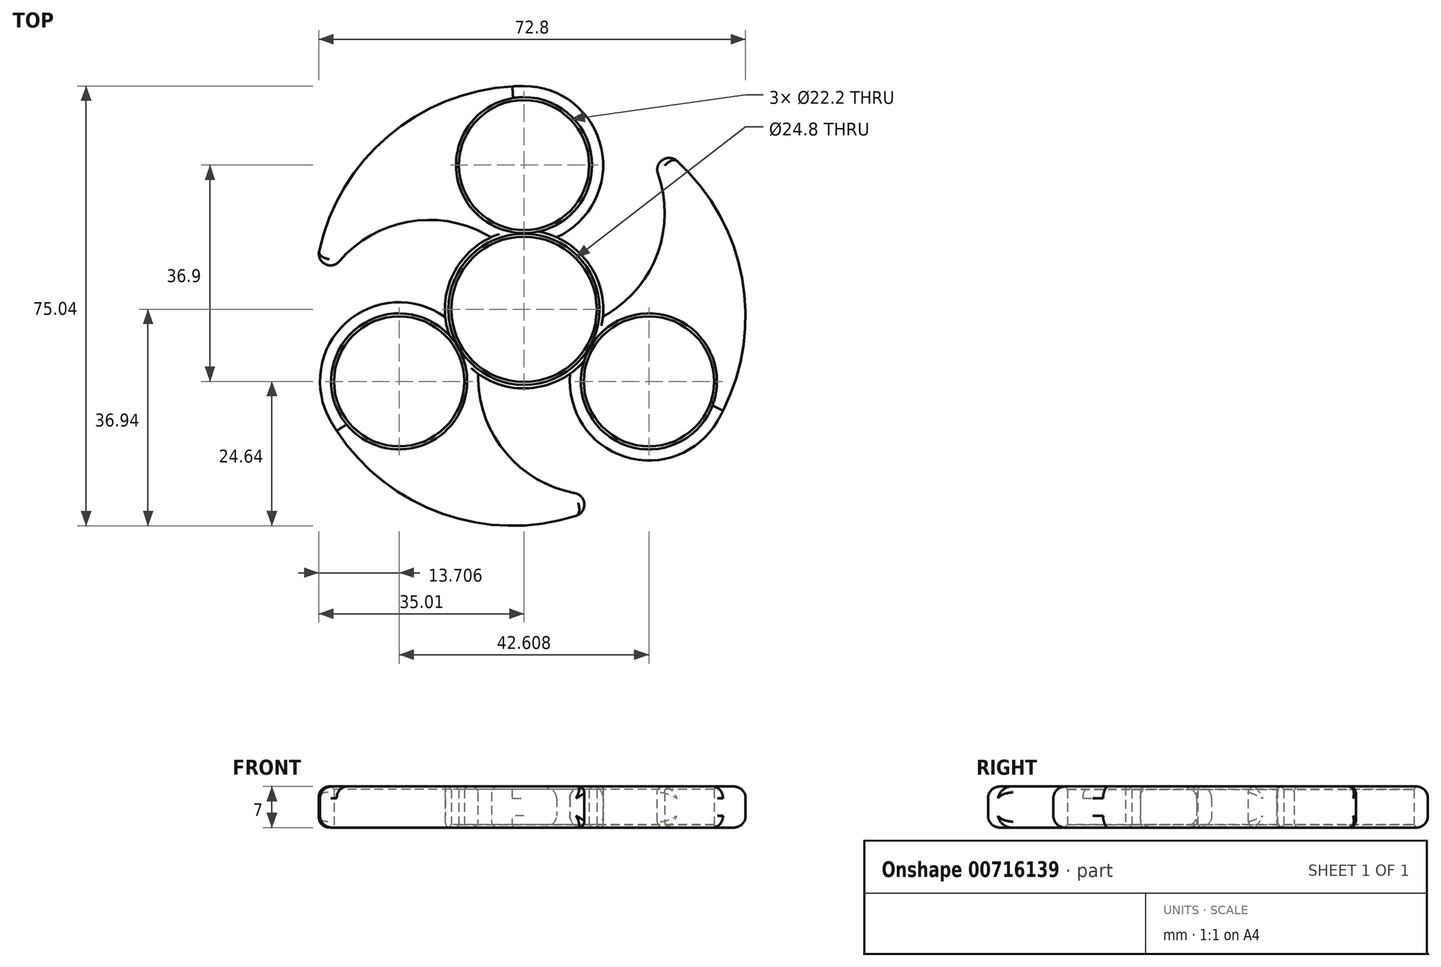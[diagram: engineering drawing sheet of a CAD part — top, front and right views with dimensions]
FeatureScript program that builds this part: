
annotation { "Feature Type Name" : "Feature", "Feature Type Description" : "" }
export const myFeature = defineFeature(function(context is Context, id is Id, definition is map)
    precondition{}
    {
        {
            var Q0;
            Q0=qCreatedBy(makeId("Top.planeOp"),FACE);
            var sketch = newSketch(context, id + "F0", { "sketchPlane" : qUnion([Q0])});
            skCircle(sketch, "E0", {"center": v(0, 0) * mm, "radius": 12.3 * mm});
            skCircle(sketch, "E1", {"center": v(0, 0) * mm, "radius": 4 * mm});
            skCircle(sketch, "E2", {"center": v(0, 0) * mm, "radius": 12.4 * mm});
            skCircle(sketch, "E3", {"center": v(0, 27.4) * mm, "radius": 11.2 * mm});
            skCircle(sketch, "E4", {"center": v(0, 0) * mm, "radius": 15 * mm});
            skCircle(sketch, "E5", {"center": v(0, 27.4) * mm, "radius": 15 * mm});
            skSolve(sketch);
        }
        {
            var Q0;
            Q0=qCreatedBy(makeId("Top.planeOp"),FACE);
            var sketch = newSketch(context, id + "F1", { "sketchPlane" : qUnion([Q0])});
            skCircle(sketch, "E6.0", {"center": v(0, 24.6) * mm, "radius": 11.1 * mm});
            skArc(sketch, "E6.1", {"start": v(5.56, 12.3) * mm, "mid": v(0, 38.1) * mm, "end": v(-5.56, 12.3) * mm});
            skArc(sketch, "E6.2", {"start": v(-5.56, 12.3) * mm, "mid": v(0, -13.5) * mm, "end": v(5.56, 12.3) * mm});
            skCircle(sketch, "E6.3", {"center": v(0, 0) * mm, "radius": 12.4 * mm});
            skSolve(sketch);
        }
        {
            var Q0;
            Q0=qSketchRegion(id+"F1",true);
            extrude(context, id + "F2", {"entities" : qUnion([Q0]), "depth" : 7 * mm, "offsetDistance" : 25 * mm});
        }
        {
            var Q0;
            Q0=makeQuery(id+"F2.opExtrude","SWEPT_BODY",BODY,{"disambiguationData":[OSD([sQuery(id+"F1.wireOp",EDGE,"E6.0"),sQuery(id+"F1.wireOp",EDGE,"E6.1"),sQuery(id+"F1.wireOp",EDGE,"E6.2"),sQuery(id+"F1.wireOp",EDGE,"E6.3")])]});
            var Q1;
            Q1=makeQuery(id+"F2.opExtrude","CAP_EDGE",EDGE,{"disambiguationData":[OSD([sQuery(id+"F1.wireOp",EDGE,"E6.3")])],"isStart":false});
            circularPattern(context, id + "F3", {"operationType" : NewBodyOperationType.ADD, "entities" : qUnion([Q0]), "axis" : qUnion([Q1]), "angle" : 360 * degree, "instanceCount" : 3, "equalSpace" : true});
        }
        {
            var Q0;
            Q0=qCreatedBy(makeId("Top.planeOp"),FACE);
            var sketch = newSketch(context, id + "F4", { "sketchPlane" : qUnion([Q0])});
            skArc(sketch, "E7", {"start": v(0, 38.1) * mm, "mid": v(-26.1, 26.79) * mm, "end": v(-35.7, 0) * mm});
            skLineSegment(sketch, "E8", {"start": v(0, 0) * mm, "end": v(0, 35.7) * mm, "construction": true});
            skLineSegment(sketch, "E9", {"start": v(0, 0) * mm, "end": v(-35.7, 0) * mm, "construction": true});
            skArc(sketch, "E10", {"start": v(-6.5, 12.77) * mm, "mid": v(-24.24, 13.57) * mm, "end": v(-35.7, 0) * mm});
            skLineSegment(sketch, "E11", {"start": v(1, 25.76) * mm, "end": v(-6.5, 12.77) * mm, "construction": true});
            skArc(sketch, "E12.0", {"start": v(0, 38.1) * mm, "mid": v(-13.08, 27.96) * mm, "end": v(-6.5, 12.77) * mm});
            skPoint(sketch, "E13.orphan", {"position": v(-5.56, 12.3) * mm});
            skPoint(sketch, "E14.orphan", {"position": v(5.56, 12.3) * mm});
            skPoint(sketch, "E15.center", {"position": v(0, 0) * mm});
            skArc(sketch, "E16.1.0", {"start": v(-7.8, -12.01) * mm, "mid": v(0.37, -27.78) * mm, "end": v(17.85, -30.92) * mm});
            skArc(sketch, "E16.1.1", {"start": v(-33, -19.05) * mm, "mid": v(-10.14, -36) * mm, "end": v(17.85, -30.92) * mm});
            skArc(sketch, "E16.2.0", {"start": v(14.3, -0.75) * mm, "mid": v(23.87, 14.2) * mm, "end": v(17.85, 30.92) * mm});
            skArc(sketch, "E16.2.1", {"start": v(33, -19.05) * mm, "mid": v(36.25, 9.22) * mm, "end": v(17.85, 30.92) * mm});
            skArc(sketch, "E17", {"start": v(33, -19.05) * mm, "mid": v(30.64, -2.77) * mm, "end": v(14.3, -0.75) * mm});
            skArc(sketch, "E18.1.0", {"start": v(0, 38.1) * mm, "mid": v(-12.92, 27.92) * mm, "end": v(-6.5, 12.77) * mm});
            skArc(sketch, "E18.2.0", {"start": v(-33, -19.05) * mm, "mid": v(-17.72, -25.15) * mm, "end": v(-7.8, -12.01) * mm});
            skLineSegment(sketch, "E19", {"start": v(13.38, -1.1) * mm, "end": v(22.3, -1.1) * mm});
            skSolve(sketch);
        }
        {
            var Q0;
            Q0=makeQuery(id+"F2.opExtrude","CAP_EDGE",EDGE,{"disambiguationData":[OSD([sQuery(id+"F1.wireOp",EDGE,"E6.0")])],"isStart":false});
            var Q1;
            Q1=makeQuery(id+"F3.opPattern","COPY",EDGE,{"derivedFrom":makeQuery(id+"F2.opExtrude","CAP_EDGE",EDGE,{"disambiguationData":[OSD([sQuery(id+"F1.wireOp",EDGE,"E6.0")])],"isStart":false}),"instanceName":"1"});
            var Q2;
            Q2=makeQuery(id+"F2.opExtrude","CAP_EDGE",EDGE,{"disambiguationData":[OSD([sQuery(id+"F1.wireOp",EDGE,"E6.3")])],"isStart":false});
            var Q3;
            Q3=makeQuery(id+"F3.opPattern","COPY",EDGE,{"derivedFrom":makeQuery(id+"F2.opExtrude","CAP_EDGE",EDGE,{"disambiguationData":[OSD([sQuery(id+"F1.wireOp",EDGE,"E6.0")])],"isStart":false}),"instanceName":"2"});
            var Q4;
            Q4=makeQuery(id+"F3.opPattern","COPY",EDGE,{"derivedFrom":makeQuery(id+"F2.opExtrude","CAP_EDGE",EDGE,{"disambiguationData":[OSD([sQuery(id+"F1.wireOp",EDGE,"E6.0")])],"isStart":true}),"instanceName":"2"});
            var Q5;
            Q5=makeQuery(id+"F2.opExtrude","CAP_EDGE",EDGE,{"disambiguationData":[OSD([sQuery(id+"F1.wireOp",EDGE,"E6.3")])],"isStart":true});
            var Q6;
            Q6=makeQuery(id+"F2.opExtrude","CAP_EDGE",EDGE,{"disambiguationData":[OSD([sQuery(id+"F1.wireOp",EDGE,"E6.0")])],"isStart":true});
            chamfer(context, id + "F5", {"entities" : qUnion([Q0, Q1, Q2, Q3, Q4, Q5, Q6]), "width" : .5 * mm, "tangentPropagation" : true});
        }
        {
            var Q0;
            Q0=makeQuery(id+"F4.imprint","IMPRINT",FACE,{"disambiguationData":[TD([[makeQuery(id+"F4.imprint","IMPRINT",EDGE,{"derivedFrom":sQuery(id+"F4.wireOp",EDGE,"E7")}),1.0]])]});
            extrude(context, id + "F6", {"entities" : qUnion([Q0]), "operationType" : NewBodyOperationType.ADD, "depth" : 7 * mm, "offsetDistance" : 25 * mm});
        }
        {
            var Q0;
            Q0 = qSketchRegion(id + "F4", true);
            extrude(context, id + "F7", {"entities" : qUnion([Q0]), "operationType" : NewBodyOperationType.ADD, "depth" : 7 * mm, "offsetDistance" : 25 * mm});
        }
        {
            var Q0;
            Q0=makeQuery(id+"F7.opExtrude","SWEPT_FACE",FACE,{"disambiguationData":[OSD([sQuery(id+"F4.wireOp",EDGE,"E16.1.1")])]});
            var Q1;
            Q1=makeQuery(id+"F7.opExtrude","SWEPT_FACE",FACE,{"disambiguationData":[OSD([sQuery(id+"F4.wireOp",EDGE,"E16.2.1")])]});
            var Q2;
            Q2=makeQuery(id+"F6.opExtrude","SWEPT_FACE",FACE,{"disambiguationData":[OSD([sQuery(id+"F4.wireOp",EDGE,"E7")])]});
            fillet(context, id + "F8", {"entities" : qUnion([Q0, Q1, Q2]), "radius" : 2 * mm, "tangentPropagation" : true, "allowEdgeOverflow" : false});
        }
        {
            var Q0;
            Q0=makeQuery(id+"F6.opExtrude","SWEPT_FACE",FACE,{"disambiguationData":[OSD([sQuery(id+"F4.wireOp",EDGE,"E10")])]});
            var Q1;
            Q1=makeQuery(id+"F7.opExtrude","SWEPT_FACE",FACE,{"disambiguationData":[OSD([sQuery(id+"F4.wireOp",EDGE,"E16.1.0")])]});
            var Q2;
            Q2=makeQuery(id+"F7.opExtrude","SWEPT_FACE",FACE,{"disambiguationData":[OSD([sQuery(id+"F4.wireOp",EDGE,"E16.2.0")])]});
            fillet(context, id + "F9", {"entities" : qUnion([Q0, Q1, Q2]), "radius" : 1 * mm, "tangentPropagation" : true, "allowEdgeOverflow" : false});
        }
    });
